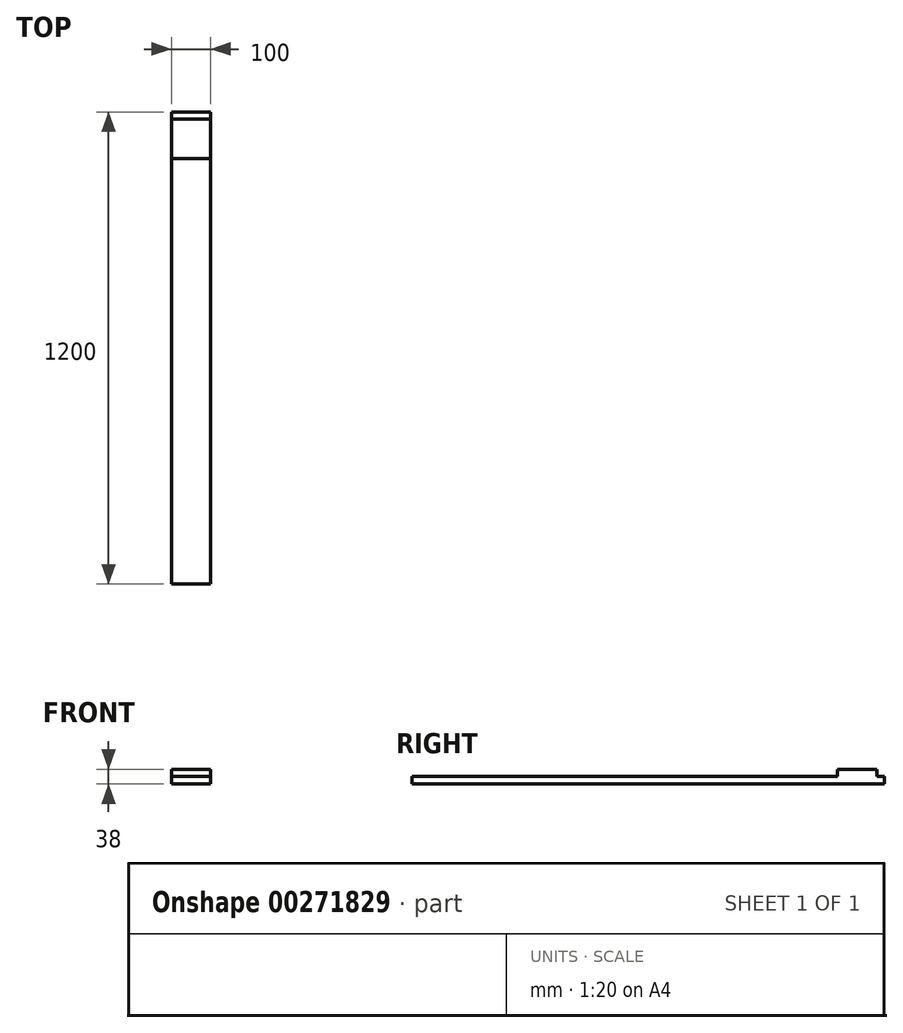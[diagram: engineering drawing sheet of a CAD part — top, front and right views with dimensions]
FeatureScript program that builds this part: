
annotation { "Feature Type Name" : "Feature", "Feature Type Description" : "" }
export const myFeature = defineFeature(function(context is Context, id is Id, definition is map)
    precondition{}
    {
        {
            var Q0;
            Q0=qCreatedBy(makeId("Front.planeOp"),FACE);
            var sketch = newSketch(context, id + "F0", { "sketchPlane" : qUnion([Q0])});
            skLineSegment(sketch, "E0.bottom", {"start": v(-46.2, -7.65) * mm, "end": v(53.8, -7.65) * mm});
            skLineSegment(sketch, "E0.top", {"start": v(-46.2, 11.35) * mm, "end": v(53.8, 11.35) * mm});
            skLineSegment(sketch, "E0.left", {"start": v(-46.2, -7.65) * mm, "end": v(-46.2, 11.35) * mm});
            skLineSegment(sketch, "E0.right", {"start": v(53.8, -7.65) * mm, "end": v(53.8, 11.35) * mm});
            skSolve(sketch);
        }
        {
            var Q0;
            Q0=makeQuery(id+"F0.imprint","IMPRINT",FACE,{"disambiguationData":[TD([[makeQuery(id+"F0.imprint","IMPRINT",EDGE,{"derivedFrom":sQuery(id+"F0.wireOp",EDGE,"E0.bottom")}),1.0]])]});
            extrude(context, id + "F1", {"entities" : qUnion([Q0]), "depth" : 1200 * mm});
        }
        {
            var Q0;
            Q0=makeQuery(id+"F1.opExtrude","SWEPT_FACE",FACE,{"disambiguationData":[OSD([sQuery(id+"F0.wireOp",EDGE,"E0.top")])]});
            var sketch = newSketch(context, id + "F2", { "sketchPlane" : qUnion([Q0])});
            skLineSegment(sketch, "E1.bottom", {"start": v(53.8, -19) * mm, "end": v(-46.2, -19) * mm});
            skLineSegment(sketch, "E1.top", {"start": v(53.8, -119) * mm, "end": v(-46.2, -119) * mm});
            skLineSegment(sketch, "E1.left", {"start": v(53.8, -19) * mm, "end": v(53.8, -119) * mm});
            skLineSegment(sketch, "E1.right", {"start": v(-46.2, -19) * mm, "end": v(-46.2, -119) * mm});
            skSolve(sketch);
        }
        {
            var Q0;
            Q0 = qSketchRegion(id + "F2", true);
            extrude(context, id + "F3", {"entities" : qUnion([Q0]), "operationType" : NewBodyOperationType.ADD, "depth" : 19 * mm});
        }
    });
